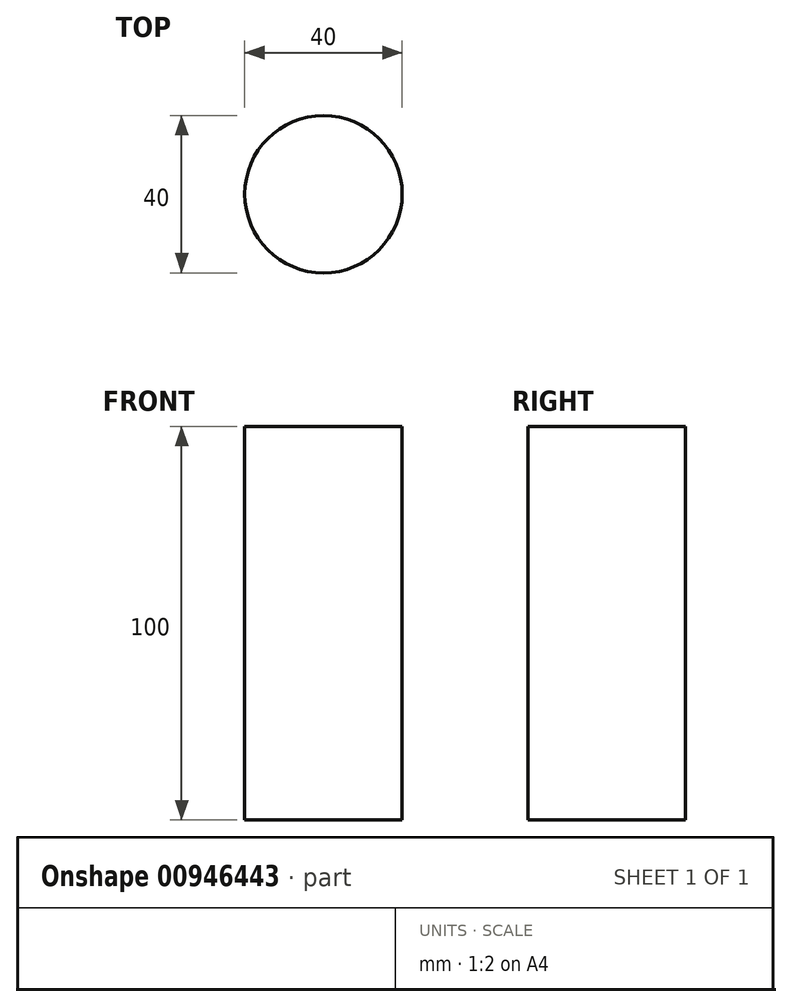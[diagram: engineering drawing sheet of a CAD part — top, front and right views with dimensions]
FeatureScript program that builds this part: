
annotation { "Feature Type Name" : "Feature", "Feature Type Description" : "" }
export const myFeature = defineFeature(function(context is Context, id is Id, definition is map)
    precondition{}
    {
        {
            var Q0;
            Q0=qCreatedBy(makeId("Top.planeOp"),FACE);
            var sketch = newSketch(context, id + "F0", { "sketchPlane" : qUnion([Q0])});
            skCircle(sketch, "E0", {"center": v(0, 0) * mm, "radius": 20 * mm});
            skSolve(sketch);
        }
        {
            var Q0;
            Q0=makeQuery(id+"F0.imprint","IMPRINT",FACE,{"disambiguationData":[TD([[makeQuery(id+"F0.imprint","IMPRINT",EDGE,{"derivedFrom":sQuery(id+"F0.wireOp",EDGE,"E0")}),1.0]])]});
            var Q1;
            Q1=sQuery(id+"F0.wireOp",EDGE,"E0");
            extrude(context, id + "F1", {"entities" : qUnion([Q0]), "bodyType" : ToolBodyType.SURFACE, "surfaceEntities" : qUnion([Q1]), "depth" : 100 * mm, "offsetDistance" : 25 * mm});
        }
    });
